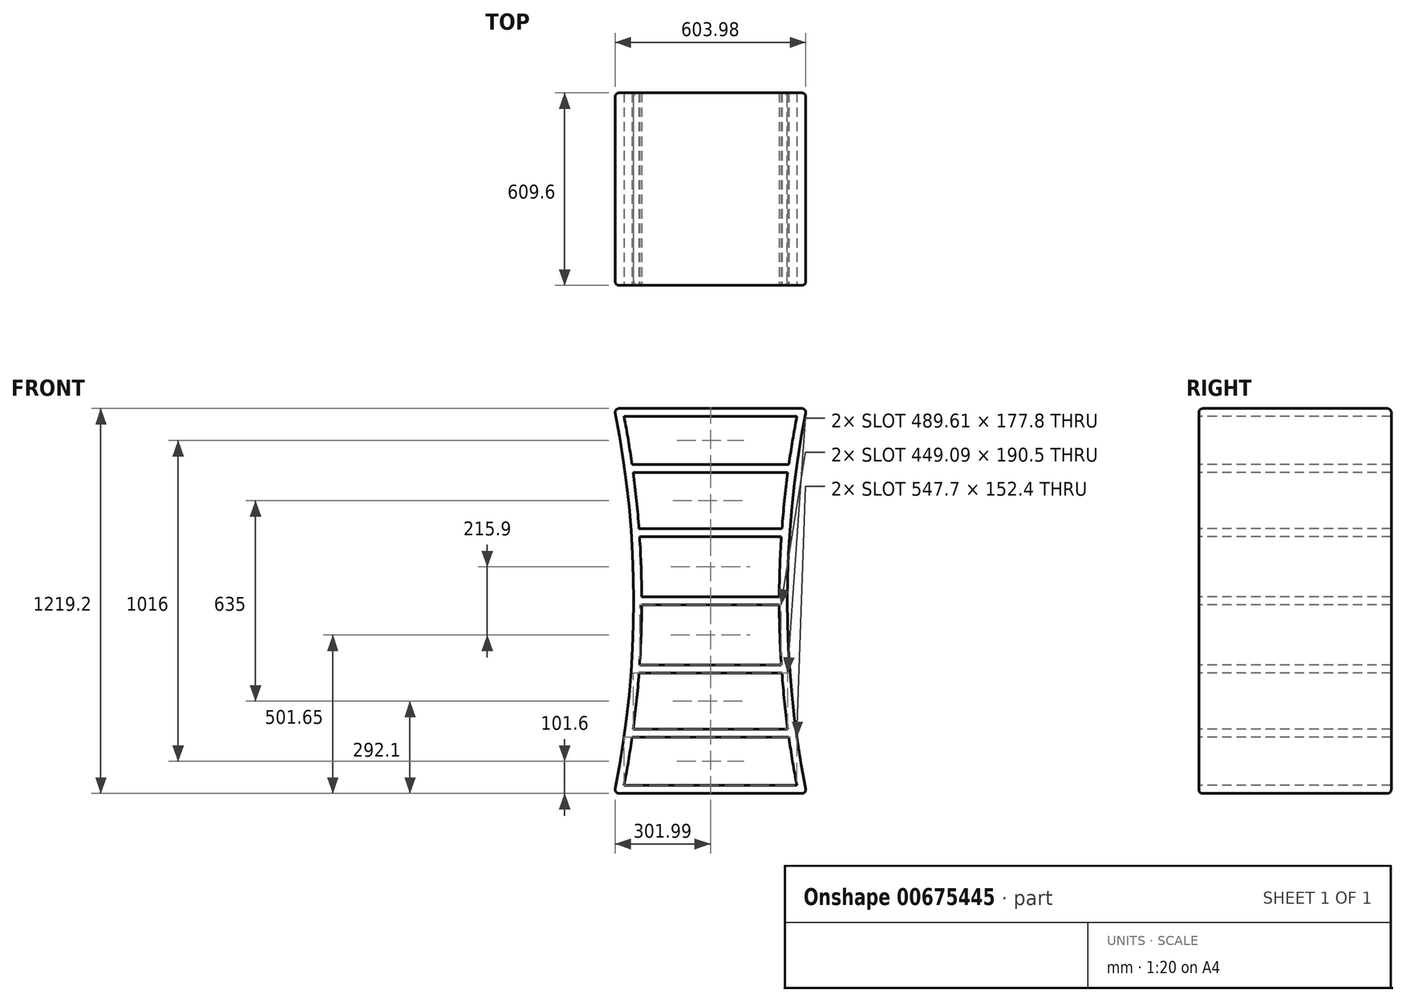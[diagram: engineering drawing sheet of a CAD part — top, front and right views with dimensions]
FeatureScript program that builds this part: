
annotation { "Feature Type Name" : "Feature", "Feature Type Description" : "" }
export const myFeature = defineFeature(function(context is Context, id is Id, definition is map)
    precondition{}
    {
        {
            var Q0;
            Q0=qCreatedBy(makeId("Front.planeOp"),FACE);
            var sketch = newSketch(context, id + "F0", { "sketchPlane" : qUnion([Q0])});
            skLineSegment(sketch, "E0.bottom", {"start": v(-304.8, 609.6) * mm, "end": v(304.8, 609.6) * mm});
            skLineSegment(sketch, "E0.top", {"start": v(-304.8, -609.6) * mm, "end": v(304.8, -609.6) * mm});
            skPoint(sketch, "E0.middle", {"position": v(0, 0) * mm});
            skArc(sketch, "E1", {"start": v(-304.8, -609.6) * mm, "mid": v(-243.22, 0) * mm, "end": v(-304.8, 609.6) * mm});
            skArc(sketch, "E2", {"start": v(304.8, 609.6) * mm, "mid": v(243.22, 0) * mm, "end": v(304.8, -609.6) * mm});
            skSolve(sketch);
        }
        {
            var Q0;
            Q0 = qSketchRegion(id + "F0", true);
            extrude(context, id + "F1", {"entities" : qUnion([Q0]), "endBound" : BoundingType.SYMMETRIC, "depth" : 609.6 * mm, "offsetDistance" : 25.4 * mm});
        }
        {
            var Q0;
            Q0=makeQuery(id+"F1.opExtrude","SWEPT_EDGE",EDGE,{"disambiguationData":[OSD([sQuery(id+"F0.wireOp",EDGE,"E0.bottom"),sQuery(id+"F0.wireOp",EDGE,"E2")])]});
            var Q1;
            Q1=makeQuery(id+"F1.opExtrude","CAP_EDGE",EDGE,{"disambiguationData":[OSD([sQuery(id+"F0.wireOp",EDGE,"E0.bottom")])],"isStart":false});
            var Q2;
            Q2=makeQuery(id+"F1.opExtrude","SWEPT_EDGE",EDGE,{"disambiguationData":[OSD([sQuery(id+"F0.wireOp",EDGE,"E0.bottom"),sQuery(id+"F0.wireOp",EDGE,"E1")])]});
            var Q3;
            Q3=makeQuery(id+"F1.opExtrude","CAP_EDGE",EDGE,{"disambiguationData":[OSD([sQuery(id+"F0.wireOp",EDGE,"E0.bottom")])],"isStart":true});
            var Q4;
            Q4=makeQuery(id+"F1.opExtrude","CAP_EDGE",EDGE,{"disambiguationData":[OSD([sQuery(id+"F0.wireOp",EDGE,"E0.top")])],"isStart":false});
            var Q5;
            Q5=makeQuery(id+"F1.opExtrude","SWEPT_EDGE",EDGE,{"disambiguationData":[OSD([sQuery(id+"F0.wireOp",EDGE,"E0.top"),sQuery(id+"F0.wireOp",EDGE,"E2")])]});
            var Q6;
            Q6=makeQuery(id+"F1.opExtrude","CAP_EDGE",EDGE,{"disambiguationData":[OSD([sQuery(id+"F0.wireOp",EDGE,"E0.top")])],"isStart":true});
            var Q7;
            Q7=makeQuery(id+"F1.opExtrude","SWEPT_EDGE",EDGE,{"disambiguationData":[OSD([sQuery(id+"F0.wireOp",EDGE,"E0.top"),sQuery(id+"F0.wireOp",EDGE,"E1")])]});
            var Q8;
            Q8=makeQuery(id+"F1.opExtrude","CAP_EDGE",EDGE,{"disambiguationData":[OSD([sQuery(id+"F0.wireOp",EDGE,"E2")])],"isStart":false});
            var Q9;
            Q9=makeQuery(id+"F1.opExtrude","CAP_EDGE",EDGE,{"disambiguationData":[OSD([sQuery(id+"F0.wireOp",EDGE,"E1")])],"isStart":false});
            var Q10;
            Q10=makeQuery(id+"F1.opExtrude","CAP_EDGE",EDGE,{"disambiguationData":[OSD([sQuery(id+"F0.wireOp",EDGE,"E2")])],"isStart":true});
            var Q11;
            Q11=makeQuery(id+"F1.opExtrude","CAP_EDGE",EDGE,{"disambiguationData":[OSD([sQuery(id+"F0.wireOp",EDGE,"E1")])],"isStart":true});
            fillet(context, id + "F2", {"entities" : qUnion([Q0, Q1, Q2, Q3, Q4, Q5, Q6, Q7, Q8, Q9, Q10, Q11]), "radius" : 12.7 * mm, "tangentPropagation" : true, "allowEdgeOverflow" : false});
        }
        {
            var Q0;
            Q0=makeQuery(id+"F1.opExtrude","CAP_FACE",FACE,{"disambiguationData":[OSD([sQuery(id+"F0.wireOp",EDGE,"E0.bottom"),sQuery(id+"F0.wireOp",EDGE,"E0.top"),sQuery(id+"F0.wireOp",EDGE,"E1"),sQuery(id+"F0.wireOp",EDGE,"E2")])],"isStart":false});
            var sketch = newSketch(context, id + "F3", { "sketchPlane" : qUnion([Q0])});
            skLineSegment(sketch, "E3.0", {"start": v(273.85, 584.2) * mm, "end": v(-273.85, 584.2) * mm});
            skArc(sketch, "E3.1", {"start": v(273.85, -584.2) * mm, "mid": v(217.82, 0) * mm, "end": v(273.85, 584.2) * mm});
            skLineSegment(sketch, "E3.2", {"start": v(-273.85, -584.2) * mm, "end": v(273.85, -584.2) * mm});
            skArc(sketch, "E3.3", {"start": v(-273.85, 584.2) * mm, "mid": v(-217.82, 0) * mm, "end": v(-273.85, -584.2) * mm});
            skLineSegment(sketch, "E4", {"start": v(-217.82, 0) * mm, "end": v(217.82, 0) * mm});
            skLineSegment(sketch, "E5", {"start": v(-217.84, 12.7) * mm, "end": v(217.84, 12.7) * mm});
            skLineSegment(sketch, "E6", {"start": v(-217.84, -12.7) * mm, "end": v(217.84, -12.7) * mm});
            skLineSegment(sketch, "E7", {"start": v(-224.54, 203.2) * mm, "end": v(224.54, 203.2) * mm});
            skLineSegment(sketch, "E8", {"start": v(-226.33, 228.6) * mm, "end": v(226.33, 228.6) * mm});
            skLineSegment(sketch, "E9", {"start": v(-248.3, 431.8) * mm, "end": v(248.3, 431.8) * mm});
            skLineSegment(sketch, "E10", {"start": v(-244.8, 406.4) * mm, "end": v(244.8, 406.4) * mm});
            skLineSegment(sketch, "E11", {"start": v(-224.54, -203.2) * mm, "end": v(224.54, -203.2) * mm});
            skLineSegment(sketch, "E12", {"start": v(-226.33, -228.6) * mm, "end": v(226.33, -228.6) * mm});
            skLineSegment(sketch, "E13", {"start": v(-244.8, -406.4) * mm, "end": v(244.8, -406.4) * mm});
            skLineSegment(sketch, "E14", {"start": v(-248.3, -431.8) * mm, "end": v(248.3, -431.8) * mm});
            skSolve(sketch);
        }
        {
            var Q0;
            {var subQ0=sQuery(id+"F3.wireOp",EDGE,"E3.0");Q0=makeQuery(id+"F3.imprint","IMPRINT",FACE,{"disambiguationData":[TD([[makeQuery(id+"F3.imprint","IMPRINT",EDGE,{"derivedFrom":subQ0}),1.0]])]});}
            var Q1;
            {var subQ0=sQuery(id+"F3.wireOp",EDGE,"E3.2");Q1=makeQuery(id+"F3.imprint","IMPRINT",FACE,{"disambiguationData":[TD([[makeQuery(id+"F3.imprint","IMPRINT",EDGE,{"derivedFrom":subQ0}),1.0]])]});}
            var Q2;
            {var subQ0=sQuery(id+"F3.wireOp",EDGE,"E12");Q2=makeQuery(id+"F3.imprint","IMPRINT",FACE,{"disambiguationData":[TD([[makeQuery(id+"F3.imprint","IMPRINT",EDGE,{"derivedFrom":subQ0}),-1.0]])]});}
            var Q3;
            {var subQ0=sQuery(id+"F3.wireOp",EDGE,"E6");Q3=makeQuery(id+"F3.imprint","IMPRINT",FACE,{"disambiguationData":[TD([[makeQuery(id+"F3.imprint","IMPRINT",EDGE,{"derivedFrom":subQ0}),-1.0]])]});}
            var Q4;
            {var subQ0=sQuery(id+"F3.wireOp",EDGE,"E5");Q4=makeQuery(id+"F3.imprint","IMPRINT",FACE,{"disambiguationData":[TD([[makeQuery(id+"F3.imprint","IMPRINT",EDGE,{"derivedFrom":subQ0}),1.0]])]});}
            var Q5;
            {var subQ0=sQuery(id+"F3.wireOp",EDGE,"E8");Q5=makeQuery(id+"F3.imprint","IMPRINT",FACE,{"disambiguationData":[TD([[makeQuery(id+"F3.imprint","IMPRINT",EDGE,{"derivedFrom":subQ0}),1.0]])]});}
            extrude(context, id + "F4", {"entities" : qUnion([Q0, Q1, Q2, Q3, Q4, Q5]), "operationType" : NewBodyOperationType.REMOVE, "endBound" : BoundingType.THROUGH_ALL, "oppositeDirection" : true, "depth" : 25.4 * mm, "offsetDistance" : 25.4 * mm});
        }
    });
